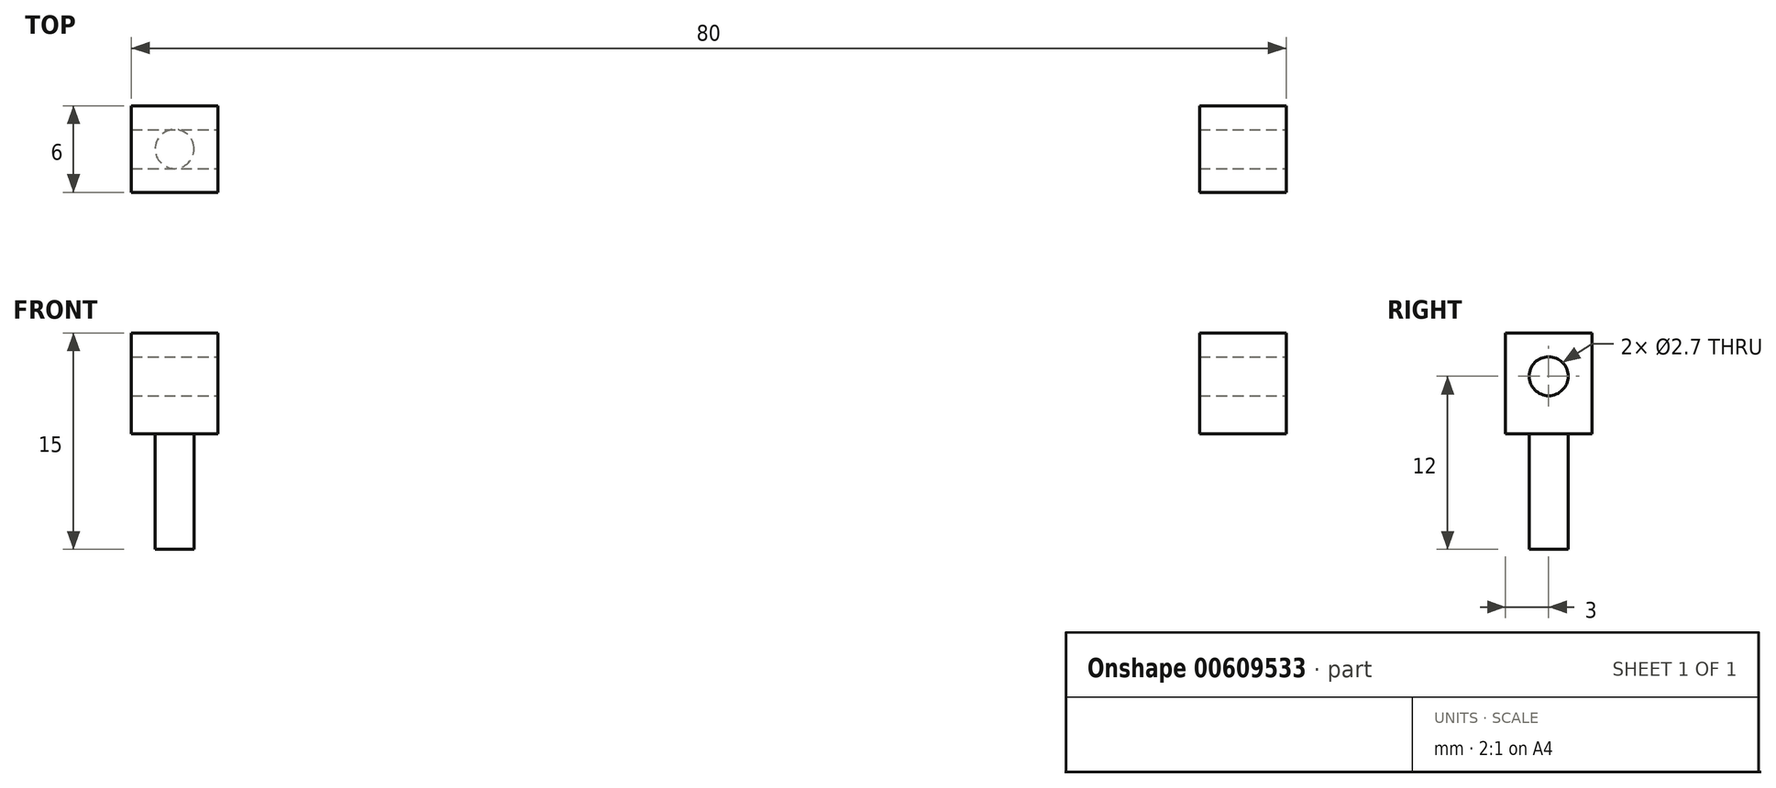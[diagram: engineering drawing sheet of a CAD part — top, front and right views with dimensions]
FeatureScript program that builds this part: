
annotation { "Feature Type Name" : "Feature", "Feature Type Description" : "" }
export const myFeature = defineFeature(function(context is Context, id is Id, definition is map)
    precondition{}
    {
        {
            var Q0;
            Q0=qCreatedBy(makeId("Top.planeOp"),FACE);
            var sketch = newSketch(context, id + "F0", { "sketchPlane" : qUnion([Q0])});
            skLineSegment(sketch, "E0.bottom", {"start": v(-34, -4.5) * mm, "end": v(-40, -4.5) * mm});
            skLineSegment(sketch, "E0.top", {"start": v(-34, 4.5) * mm, "end": v(-40, 4.5) * mm});
            skLineSegment(sketch, "E0.left", {"start": v(-34, -4.5) * mm, "end": v(-34, 1.5) * mm});
            skLineSegment(sketch, "E0.right", {"start": v(-40, -4.5) * mm, "end": v(-40, 4.5) * mm});
            skPoint(sketch, "E0.middle", {"position": v(-37, 0) * mm});
            skLineSegment(sketch, "E1", {"start": v(-34, 4.5) * mm, "end": v(0, 4.5) * mm});
            skLineSegment(sketch, "E2", {"start": v(0, 1.5) * mm, "end": v(-34, 1.5) * mm});
            skLineSegment(sketch, "E3.MirrorCS", {"start": v(34, 4.5) * mm, "end": v(0, 4.5) * mm});
            skLineSegment(sketch, "E4.MirrorCS", {"start": v(0, 1.5) * mm, "end": v(34, 1.5) * mm});
            skLineSegment(sketch, "E5.MirrorCS", {"start": v(34, 4.5) * mm, "end": v(40, 4.5) * mm});
            skLineSegment(sketch, "E6.MirrorCS", {"start": v(40, -4.5) * mm, "end": v(40, 4.5) * mm});
            skLineSegment(sketch, "E7.MirrorCS", {"start": v(34, -4.5) * mm, "end": v(40, -4.5) * mm});
            skLineSegment(sketch, "E8.MirrorCS", {"start": v(34, -4.5) * mm, "end": v(34, 1.5) * mm});
            skSolve(sketch);
        }
        {
            var Q0;
            Q0=makeQuery(id+"F0.imprint","IMPRINT",FACE,{"disambiguationData":[TD([[makeQuery(id+"F0.imprint","IMPRINT",EDGE,{"derivedFrom":sQuery(id+"F0.wireOp",EDGE,"E0.bottom")}),-1.0]])]});
            extrude(context, id + "F1", {"entities" : qUnion([Q0]), "depth" : 15 * mm, "offsetDistance" : 25 * mm});
        }
        {
            var Q0;
            Q0=makeQuery(id+"F1.opExtrude","CAP_FACE",FACE,{"disambiguationData":[OSD([sQuery(id+"F0.wireOp",EDGE,"E0.bottom"),sQuery(id+"F0.wireOp",EDGE,"E0.top"),sQuery(id+"F0.wireOp",EDGE,"E0.left"),sQuery(id+"F0.wireOp",EDGE,"E0.right"),sQuery(id+"F0.wireOp",EDGE,"E1"),sQuery(id+"F0.wireOp",EDGE,"E2"),sQuery(id+"F0.wireOp",EDGE,"E3.MirrorCS"),sQuery(id+"F0.wireOp",EDGE,"E4.MirrorCS"),sQuery(id+"F0.wireOp",EDGE,"E5.MirrorCS"),sQuery(id+"F0.wireOp",EDGE,"E6.MirrorCS"),sQuery(id+"F0.wireOp",EDGE,"E7.MirrorCS"),sQuery(id+"F0.wireOp",EDGE,"E8.MirrorCS")])],"isStart":false});
            var sketch = newSketch(context, id + "F2", { "sketchPlane" : qUnion([Q0])});
            skLineSegment(sketch, "E9", {"start": v(-34, 1.5) * mm, "end": v(-34, 4.5) * mm});
            skLineSegment(sketch, "E10", {"start": v(-34, 4.5) * mm, "end": v(34, 4.5) * mm});
            skLineSegment(sketch, "E11", {"start": v(34, 4.5) * mm, "end": v(34, 1.5) * mm});
            skLineSegment(sketch, "E12", {"start": v(34, 1.5) * mm, "end": v(-34, 1.5) * mm});
            skSolve(sketch);
        }
        {
            var Q0;
            Q0=makeQuery(id+"F2.imprint","IMPRINT",FACE,{"disambiguationData":[TD([[makeQuery(id+"F2.imprint","IMPRINT",EDGE,{"derivedFrom":sQuery(id+"F2.wireOp",EDGE,"E9")}),-1.0]])]});
            extrude(context, id + "F3", {"entities" : qUnion([Q0]), "operationType" : NewBodyOperationType.REMOVE, "oppositeDirection" : true, "depth" : 10 * mm, "offsetDistance" : 25 * mm});
        }
        {
            var Q0;
            Q0=makeQuery(id+"F1.opExtrude","CAP_FACE",FACE,{"disambiguationData":[OSD([sQuery(id+"F0.wireOp",EDGE,"E0.bottom"),sQuery(id+"F0.wireOp",EDGE,"E0.top"),sQuery(id+"F0.wireOp",EDGE,"E0.left"),sQuery(id+"F0.wireOp",EDGE,"E0.right"),sQuery(id+"F0.wireOp",EDGE,"E1"),sQuery(id+"F0.wireOp",EDGE,"E2"),sQuery(id+"F0.wireOp",EDGE,"E3.MirrorCS"),sQuery(id+"F0.wireOp",EDGE,"E4.MirrorCS"),sQuery(id+"F0.wireOp",EDGE,"E5.MirrorCS"),sQuery(id+"F0.wireOp",EDGE,"E6.MirrorCS"),sQuery(id+"F0.wireOp",EDGE,"E7.MirrorCS"),sQuery(id+"F0.wireOp",EDGE,"E8.MirrorCS")])],"isStart":true});
            var sketch = newSketch(context, id + "F4", { "sketchPlane" : qUnion([Q0])});
            skCircle(sketch, "E13", {"center": v(37, 1.5) * mm, "radius": 1.35 * mm});
            skCircle(sketch, "E14.MirrorC", {"center": v(-37, 1.5) * mm, "radius": 1.35 * mm});
            skSolve(sketch);
        }
        {
            var Q0;
            Q0=makeQuery(id+"F4.imprint","IMPRINT",FACE,{"disambiguationData":[TD([[makeQuery(id+"F4.imprint","IMPRINT",EDGE,{"derivedFrom":sQuery(id+"F4.wireOp",EDGE,"E13")}),1.0]])]});
            var Q1;
            Q1=makeQuery(id+"F4.imprint","IMPRINT",FACE,{"disambiguationData":[TD([[makeQuery(id+"F4.imprint","IMPRINT",EDGE,{"derivedFrom":sQuery(id+"F4.wireOp",EDGE,"E14.MirrorC")}),-1.0]])]});
            extrude(context, id + "F5", {"entities" : qUnion([Q0, Q1]), "operationType" : NewBodyOperationType.REMOVE, "oppositeDirection" : true, "depth" : 8 * mm, "offsetDistance" : 25 * mm});
        }
        {
            var Q0;
            Q0=makeQuery(id+"F1.opExtrude","SWEPT_FACE",FACE,{"disambiguationData":[OSD([sQuery(id+"F0.wireOp",EDGE,"E6.MirrorCS")])]});
            var sketch = newSketch(context, id + "F6", { "sketchPlane" : qUnion([Q0])});
            skCircle(sketch, "E15", {"center": v(-1.5, 12) * mm, "radius": 1.35 * mm});
            skLineSegment(sketch, "E16", {"start": v(1.5, 15) * mm, "end": v(1.5, 5) * mm});
            skLineSegment(sketch, "E17", {"start": v(1.5, 5) * mm, "end": v(4.5, 5) * mm});
            skSolve(sketch);
        }
        {
            var Q0;
            {var subQ0=sQuery(id+"F6.wireOp",EDGE,"E16");Q0=makeQuery(id+"F6.imprint","IMPRINT",FACE,{"disambiguationData":[TD([[makeQuery(id+"F6.imprint","IMPRINT",EDGE,{"derivedFrom":subQ0}),1.0]])]});}
            var Q1;
            Q1=makeQuery(id+"F6.imprint","IMPRINT",FACE,{"disambiguationData":[TD([[makeQuery(id+"F6.imprint","IMPRINT",EDGE,{"derivedFrom":sQuery(id+"F6.wireOp",EDGE,"E15")}),1.0]])]});
            extrude(context, id + "F7", {"entities" : qUnion([Q0, Q1]), "operationType" : NewBodyOperationType.REMOVE, "endBound" : BoundingType.THROUGH_ALL, "oppositeDirection" : true, "depth" : 25 * mm, "offsetDistance" : 25 * mm});
        }
    });
